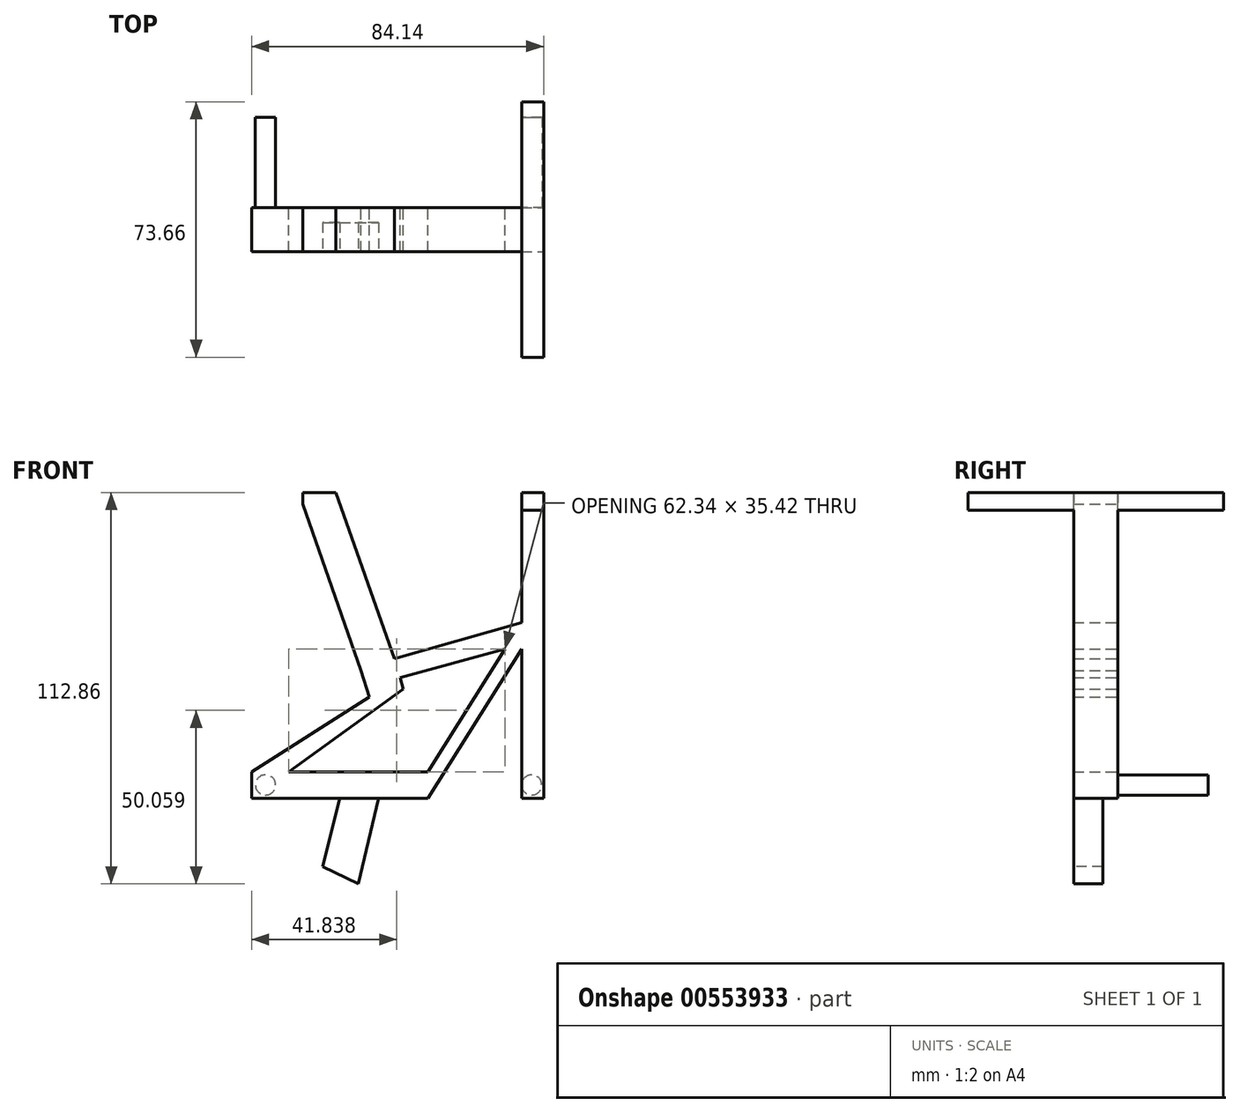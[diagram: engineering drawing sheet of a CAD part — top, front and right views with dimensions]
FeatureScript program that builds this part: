
annotation { "Feature Type Name" : "Feature", "Feature Type Description" : "" }
export const myFeature = defineFeature(function(context is Context, id is Id, definition is map)
    precondition{}
    {
        {
            var Q0;
            Q0=qCreatedBy(makeId("Front.planeOp"),FACE);
            var sketch = newSketch(context, id + "F0", { "sketchPlane" : qUnion([Q0])});
            skLineSegment(sketch, "E0", {"start": v(0, 0) * mm, "end": v(50.8, 0) * mm});
            skLineSegment(sketch, "E1", {"start": v(0, 0) * mm, "end": v(0, 7.62) * mm});
            skLineSegment(sketch, "E2", {"start": v(0, 7.62) * mm, "end": v(50.8, 7.62) * mm});
            skLineSegment(sketch, "E3", {"start": v(50.8, 7.62) * mm, "end": v(50.8, 0) * mm});
            skLineSegment(sketch, "E4", {"start": v(50.8, 7.62) * mm, "end": v(77.79, 50.66) * mm});
            skLineSegment(sketch, "E5", {"start": v(50.8, 0) * mm, "end": v(77.79, 43.04) * mm});
            skLineSegment(sketch, "E6", {"start": v(77.79, 43.04) * mm, "end": v(77.79, 50.66) * mm});
            skLineSegment(sketch, "E7", {"start": v(77.79, 50.66) * mm, "end": v(41.14, 40.22) * mm});
            skLineSegment(sketch, "E8", {"start": v(73, 43.04) * mm, "end": v(41.14, 34.38) * mm});
            skLineSegment(sketch, "E9", {"start": v(41.14, 34.38) * mm, "end": v(41.14, 40.22) * mm});
            skLineSegment(sketch, "E10", {"start": v(42.88, 34.85) * mm, "end": v(0, 7.62) * mm});
            skLineSegment(sketch, "E11", {"start": v(51.9, 37.3) * mm, "end": v(10.67, 7.62) * mm});
            skPoint(sketch, "E11.startSnap0", {"position": v(41.14, 37.3) * mm});
            skLineSegment(sketch, "E12", {"start": v(50.8, 7.62) * mm, "end": v(41.14, 40.22) * mm});
            skLineSegment(sketch, "E13", {"start": v(40.22, 7.62) * mm, "end": v(31.56, 36.85) * mm});
            skLineSegment(sketch, "E14", {"start": v(31.56, 36.85) * mm, "end": v(41.14, 40.22) * mm});
            skLineSegment(sketch, "E15", {"start": v(31.56, 36.85) * mm, "end": v(14.68, 84.76) * mm});
            skLineSegment(sketch, "E16", {"start": v(14.68, 84.76) * mm, "end": v(24.26, 88.13) * mm});
            skLineSegment(sketch, "E17", {"start": v(24.26, 88.13) * mm, "end": v(41.14, 40.22) * mm});
            skLineSegment(sketch, "E18.bottom", {"start": v(14.68, 84.76) * mm, "end": v(24.26, 84.76) * mm});
            skLineSegment(sketch, "E18.top", {"start": v(14.68, 88.13) * mm, "end": v(24.26, 88.13) * mm});
            skLineSegment(sketch, "E18.left", {"start": v(14.68, 84.76) * mm, "end": v(14.68, 88.13) * mm});
            skLineSegment(sketch, "E18.right", {"start": v(24.26, 84.76) * mm, "end": v(24.26, 88.13) * mm});
            skSolve(sketch);
        }
        {
            var Q0;
            Q0 = qSketchRegion(id + "F0", true);
            extrude(context, id + "F1", {"entities" : qUnion([Q0]), "depth" : 12.7 * mm, "offsetDistance" : 25.4 * mm});
        }
        {
            var Q0;
            Q0=makeQuery(id+"F1.opExtrude","SWEPT_FACE",FACE,{"disambiguationData":[OSD([sQuery(id+"F0.wireOp",EDGE,"E6")])]});
            var sketch = newSketch(context, id + "F2", { "sketchPlane" : qUnion([Q0])});
            skPoint(sketch, "E19.oppositeSnap0", {"position": v(-12.7, 46.85) * mm});
            skLineSegment(sketch, "E20.bottom", {"start": v(-12.7, 43.04) * mm, "end": v(0, 43.04) * mm});
            skLineSegment(sketch, "E20.top", {"start": v(-12.7, 88.13) * mm, "end": v(0, 88.13) * mm});
            skLineSegment(sketch, "E20.left", {"start": v(-12.7, 43.04) * mm, "end": v(-12.7, 88.13) * mm});
            skLineSegment(sketch, "E20.right", {"start": v(0, 43.04) * mm, "end": v(0, 88.13) * mm});
            skLineSegment(sketch, "E21.bottom", {"start": v(0, 88.13) * mm, "end": v(30.48, 88.13) * mm});
            skLineSegment(sketch, "E21.top", {"start": v(0, 83.05) * mm, "end": v(30.48, 83.05) * mm});
            skLineSegment(sketch, "E21.left", {"start": v(0, 88.13) * mm, "end": v(0, 83.05) * mm});
            skLineSegment(sketch, "E21.right", {"start": v(30.48, 88.13) * mm, "end": v(30.48, 83.05) * mm});
            skLineSegment(sketch, "E22.bottom", {"start": v(-12.7, 88.13) * mm, "end": v(-43.18, 88.13) * mm});
            skLineSegment(sketch, "E22.top", {"start": v(-12.7, 83.05) * mm, "end": v(-43.18, 83.05) * mm});
            skLineSegment(sketch, "E22.left", {"start": v(-12.7, 88.13) * mm, "end": v(-12.7, 83.05) * mm});
            skLineSegment(sketch, "E22.right", {"start": v(-43.18, 88.13) * mm, "end": v(-43.18, 83.05) * mm});
            skSolve(sketch);
        }
        {
            var Q0;
            Q0 = qSketchRegion(id + "F2", true);
            extrude(context, id + "F3", {"entities" : qUnion([Q0]), "operationType" : NewBodyOperationType.ADD, "depth" : 6.35 * mm, "offsetDistance" : 25.4 * mm});
        }
        {
            var Q0;
            Q0=makeQuery(id+"F3.boolean.opBoolean","MERGE",FACE,{"derivedFrom":[makeQuery(id+"F1.opExtrude","CAP_FACE",FACE,{"disambiguationData":[OSD([sQuery(id+"F0.wireOp",EDGE,"E0"),sQuery(id+"F0.wireOp",EDGE,"E1"),sQuery(id+"F0.wireOp",EDGE,"E2"),sQuery(id+"F0.wireOp",EDGE,"E4"),sQuery(id+"F0.wireOp",EDGE,"E5"),sQuery(id+"F0.wireOp",EDGE,"E6"),sQuery(id+"F0.wireOp",EDGE,"E7"),sQuery(id+"F0.wireOp",EDGE,"E8"),sQuery(id+"F0.wireOp",EDGE,"E10"),sQuery(id+"F0.wireOp",EDGE,"E11"),sQuery(id+"F0.wireOp",EDGE,"E12"),sQuery(id+"F0.wireOp",EDGE,"E13"),sQuery(id+"F0.wireOp",EDGE,"E15"),sQuery(id+"F0.wireOp",EDGE,"E17"),sQuery(id+"F0.wireOp",EDGE,"E18.top"),sQuery(id+"F0.wireOp",EDGE,"E18.left")])],"isStart":true}),makeQuery(id+"F3.opExtrude","SWEPT_FACE",FACE,{"disambiguationData":[OSD([sQuery(id+"F2.wireOp",EDGE,"E20.right")])]})]});
            var sketch = newSketch(context, id + "F4", { "sketchPlane" : qUnion([Q0])});
            skCircle(sketch, "E23", {"center": v(-4, 3.81) * mm, "radius": 2.92 * mm});
            skSolve(sketch);
        }
        {
            var Q0;
            Q0=makeQuery(id+"F4.imprint","IMPRINT",FACE,{"disambiguationData":[TD([[makeQuery(id+"F4.imprint","IMPRINT",EDGE,{"derivedFrom":sQuery(id+"F4.wireOp",EDGE,"E23")}),1.0]])]});
            extrude(context, id + "F5", {"entities" : qUnion([Q0]), "operationType" : NewBodyOperationType.ADD, "depth" : 26.03 * mm, "offsetDistance" : 25.4 * mm});
        }
        {
            var Q0;
            Q0=makeQuery(id+"F3.boolean.opBoolean","MERGE",FACE,{"derivedFrom":[makeQuery(id+"F1.opExtrude","CAP_FACE",FACE,{"disambiguationData":[OSD([sQuery(id+"F0.wireOp",EDGE,"E0"),sQuery(id+"F0.wireOp",EDGE,"E1"),sQuery(id+"F0.wireOp",EDGE,"E2"),sQuery(id+"F0.wireOp",EDGE,"E4"),sQuery(id+"F0.wireOp",EDGE,"E5"),sQuery(id+"F0.wireOp",EDGE,"E6"),sQuery(id+"F0.wireOp",EDGE,"E7"),sQuery(id+"F0.wireOp",EDGE,"E8"),sQuery(id+"F0.wireOp",EDGE,"E10"),sQuery(id+"F0.wireOp",EDGE,"E11"),sQuery(id+"F0.wireOp",EDGE,"E12"),sQuery(id+"F0.wireOp",EDGE,"E13"),sQuery(id+"F0.wireOp",EDGE,"E15"),sQuery(id+"F0.wireOp",EDGE,"E17"),sQuery(id+"F0.wireOp",EDGE,"E18.top"),sQuery(id+"F0.wireOp",EDGE,"E18.left")])],"isStart":false}),makeQuery(id+"F3.opExtrude","SWEPT_FACE",FACE,{"disambiguationData":[OSD([sQuery(id+"F2.wireOp",EDGE,"E20.left")])]})]});
            var sketch = newSketch(context, id + "F6", { "sketchPlane" : qUnion([Q0])});
            skLineSegment(sketch, "E24.bottom", {"start": v(77.79, 43.04) * mm, "end": v(84.14, 43.04) * mm});
            skLineSegment(sketch, "E24.top", {"start": v(77.79, 0) * mm, "end": v(84.14, 0) * mm});
            skLineSegment(sketch, "E24.left", {"start": v(77.79, 43.04) * mm, "end": v(77.79, 0) * mm});
            skLineSegment(sketch, "E24.right", {"start": v(84.14, 43.04) * mm, "end": v(84.14, 0) * mm});
            skSolve(sketch);
        }
        {
            var Q0;
            Q0=makeQuery(id+"F6.imprint","IMPRINT",FACE,{"disambiguationData":[TD([[makeQuery(id+"F6.imprint","IMPRINT",EDGE,{"derivedFrom":sQuery(id+"F6.wireOp",EDGE,"E24.bottom")}),1.0]])]});
            var Q1;
            Q1=makeQuery(id+"F3.boolean.opBoolean","MERGE",FACE,{"derivedFrom":[makeQuery(id+"F1.opExtrude","CAP_FACE",FACE,{"disambiguationData":[OSD([sQuery(id+"F0.wireOp",EDGE,"E0"),sQuery(id+"F0.wireOp",EDGE,"E1"),sQuery(id+"F0.wireOp",EDGE,"E2"),sQuery(id+"F0.wireOp",EDGE,"E4"),sQuery(id+"F0.wireOp",EDGE,"E5"),sQuery(id+"F0.wireOp",EDGE,"E6"),sQuery(id+"F0.wireOp",EDGE,"E7"),sQuery(id+"F0.wireOp",EDGE,"E8"),sQuery(id+"F0.wireOp",EDGE,"E10"),sQuery(id+"F0.wireOp",EDGE,"E11"),sQuery(id+"F0.wireOp",EDGE,"E12"),sQuery(id+"F0.wireOp",EDGE,"E13"),sQuery(id+"F0.wireOp",EDGE,"E15"),sQuery(id+"F0.wireOp",EDGE,"E17"),sQuery(id+"F0.wireOp",EDGE,"E18.top"),sQuery(id+"F0.wireOp",EDGE,"E18.left")])],"isStart":true}),makeQuery(id+"F3.opExtrude","SWEPT_FACE",FACE,{"disambiguationData":[OSD([sQuery(id+"F2.wireOp",EDGE,"E20.right")])]})]});
            var Q2;
            Q2=makeQuery(id+"F1.opExtrude","SWEPT_BODY",BODY,{"disambiguationData":[OSD([sQuery(id+"F0.wireOp",EDGE,"E0"),sQuery(id+"F0.wireOp",EDGE,"E1"),sQuery(id+"F0.wireOp",EDGE,"E2"),sQuery(id+"F0.wireOp",EDGE,"E4"),sQuery(id+"F0.wireOp",EDGE,"E5"),sQuery(id+"F0.wireOp",EDGE,"E6"),sQuery(id+"F0.wireOp",EDGE,"E7"),sQuery(id+"F0.wireOp",EDGE,"E8"),sQuery(id+"F0.wireOp",EDGE,"E10"),sQuery(id+"F0.wireOp",EDGE,"E11"),sQuery(id+"F0.wireOp",EDGE,"E12"),sQuery(id+"F0.wireOp",EDGE,"E13"),sQuery(id+"F0.wireOp",EDGE,"E15"),sQuery(id+"F0.wireOp",EDGE,"E17"),sQuery(id+"F0.wireOp",EDGE,"E18.top"),sQuery(id+"F0.wireOp",EDGE,"E18.left")])]});
            extrude(context, id + "F7", {"entities" : qUnion([Q0]), "operationType" : NewBodyOperationType.ADD, "endBound" : BoundingType.UP_TO_SURFACE, "oppositeDirection" : true, "depth" : 25.4 * mm, "endBoundEntityFace" : qUnion([Q1]), "endBoundEntityBody" : qUnion([Q2]), "offsetDistance" : 25.4 * mm});
        }
        {
            var Q0;
            Q0=makeQuery(id+"F7.boolean.opBoolean","MERGE",FACE,{"derivedFrom":[makeQuery(id+"F3.boolean.opBoolean","MERGE",FACE,{"derivedFrom":[makeQuery(id+"F1.opExtrude","CAP_FACE",FACE,{"disambiguationData":[OSD([sQuery(id+"F0.wireOp",EDGE,"E0"),sQuery(id+"F0.wireOp",EDGE,"E1"),sQuery(id+"F0.wireOp",EDGE,"E2"),sQuery(id+"F0.wireOp",EDGE,"E4"),sQuery(id+"F0.wireOp",EDGE,"E5"),sQuery(id+"F0.wireOp",EDGE,"E6"),sQuery(id+"F0.wireOp",EDGE,"E7"),sQuery(id+"F0.wireOp",EDGE,"E8"),sQuery(id+"F0.wireOp",EDGE,"E10"),sQuery(id+"F0.wireOp",EDGE,"E11"),sQuery(id+"F0.wireOp",EDGE,"E12"),sQuery(id+"F0.wireOp",EDGE,"E13"),sQuery(id+"F0.wireOp",EDGE,"E15"),sQuery(id+"F0.wireOp",EDGE,"E17"),sQuery(id+"F0.wireOp",EDGE,"E18.top"),sQuery(id+"F0.wireOp",EDGE,"E18.left")])],"isStart":true}),makeQuery(id+"F3.opExtrude","SWEPT_FACE",FACE,{"disambiguationData":[OSD([sQuery(id+"F2.wireOp",EDGE,"E20.right")])]})]}),makeQuery(id+"F7.opExtrude","CAP_FACE",FACE,{"disambiguationData":[OSD([sQuery(id+"F6.wireOp",EDGE,"E24.bottom"),sQuery(id+"F6.wireOp",EDGE,"E24.top"),sQuery(id+"F6.wireOp",EDGE,"E24.left"),sQuery(id+"F6.wireOp",EDGE,"E24.right")])],"isStart":false})]});
            var sketch = newSketch(context, id + "F8", { "sketchPlane" : qUnion([Q0])});
            skCircle(sketch, "E25", {"center": v(-80.7, 3.81) * mm, "radius": 2.92 * mm});
            skSolve(sketch);
        }
        {
            var Q0;
            Q0=makeQuery(id+"F8.imprint","IMPRINT",FACE,{"disambiguationData":[TD([[makeQuery(id+"F8.imprint","IMPRINT",EDGE,{"derivedFrom":sQuery(id+"F8.wireOp",EDGE,"E25")}),1.0]])]});
            extrude(context, id + "F9", {"entities" : qUnion([Q0]), "operationType" : NewBodyOperationType.ADD, "depth" : 26.03 * mm, "offsetDistance" : 25.4 * mm});
        }
        {
            var Q0;
            Q0=makeQuery(id+"F7.boolean.opBoolean","MERGE",FACE,{"derivedFrom":[makeQuery(id+"F3.boolean.opBoolean","MERGE",FACE,{"derivedFrom":[makeQuery(id+"F1.opExtrude","CAP_FACE",FACE,{"disambiguationData":[OSD([sQuery(id+"F0.wireOp",EDGE,"E0"),sQuery(id+"F0.wireOp",EDGE,"E1"),sQuery(id+"F0.wireOp",EDGE,"E2"),sQuery(id+"F0.wireOp",EDGE,"E4"),sQuery(id+"F0.wireOp",EDGE,"E5"),sQuery(id+"F0.wireOp",EDGE,"E6"),sQuery(id+"F0.wireOp",EDGE,"E7"),sQuery(id+"F0.wireOp",EDGE,"E8"),sQuery(id+"F0.wireOp",EDGE,"E10"),sQuery(id+"F0.wireOp",EDGE,"E11"),sQuery(id+"F0.wireOp",EDGE,"E12"),sQuery(id+"F0.wireOp",EDGE,"E13"),sQuery(id+"F0.wireOp",EDGE,"E15"),sQuery(id+"F0.wireOp",EDGE,"E17"),sQuery(id+"F0.wireOp",EDGE,"E18.top"),sQuery(id+"F0.wireOp",EDGE,"E18.left")])],"isStart":false}),makeQuery(id+"F3.opExtrude","SWEPT_FACE",FACE,{"disambiguationData":[OSD([sQuery(id+"F2.wireOp",EDGE,"E20.left")])]})]}),makeQuery(id+"F7.opExtrude","CAP_FACE",FACE,{"disambiguationData":[OSD([sQuery(id+"F6.wireOp",EDGE,"E24.bottom"),sQuery(id+"F6.wireOp",EDGE,"E24.top"),sQuery(id+"F6.wireOp",EDGE,"E24.left"),sQuery(id+"F6.wireOp",EDGE,"E24.right")])],"isStart":true})]});
            var sketch = newSketch(context, id + "F10", { "sketchPlane" : qUnion([Q0])});
            skLineSegment(sketch, "E26", {"start": v(36.52, 0) * mm, "end": v(30.73, -24.73) * mm});
            skPoint(sketch, "E26.endSnap0", {"position": v(30.73, 7.62) * mm});
            skLineSegment(sketch, "E27", {"start": v(25.4, 0) * mm, "end": v(20.47, -19.71) * mm});
            skLineSegment(sketch, "E28", {"start": v(20.47, -19.71) * mm, "end": v(30.73, -24.73) * mm});
            skSolve(sketch);
        }
        {
            var Q0;
            {var subQ0=sQuery(id+"F10.wireOp",EDGE,"E26");Q0=makeQuery(id+"F10.imprint","IMPRINT",FACE,{"disambiguationData":[TD([[makeQuery(id+"F10.imprint","IMPRINT",EDGE,{"derivedFrom":subQ0}),-1.0]])]});}
            extrude(context, id + "F11", {"entities" : qUnion([Q0]), "oppositeDirection" : true, "depth" : 8.38 * mm, "offsetDistance" : 25.4 * mm});
        }
    });
